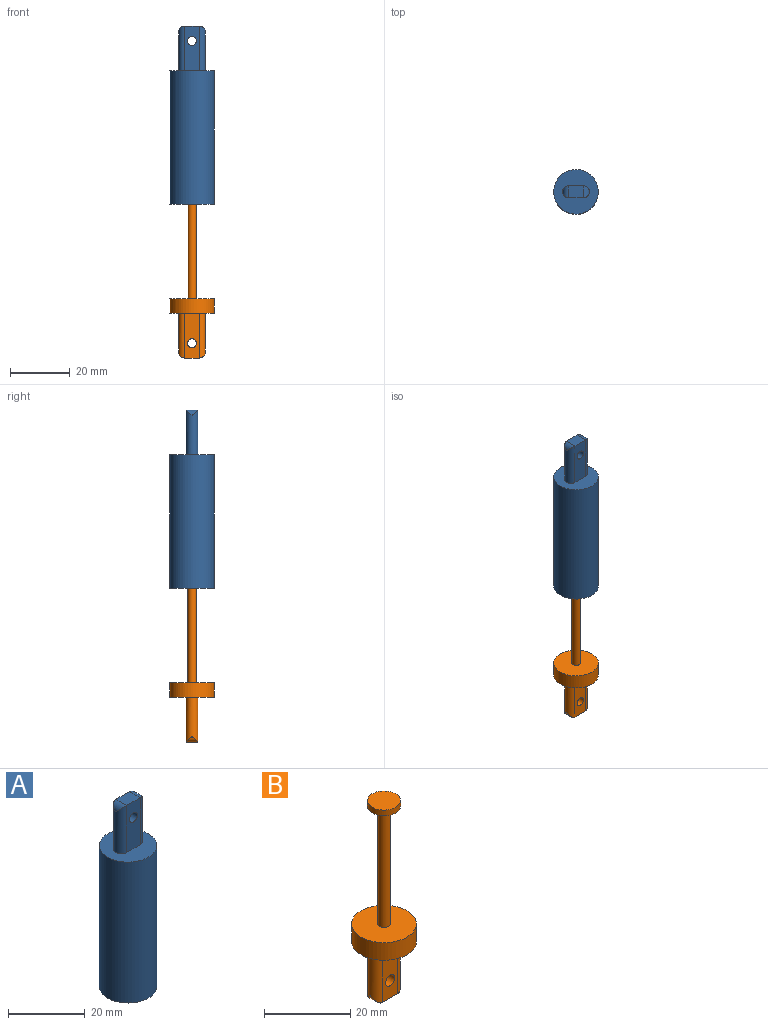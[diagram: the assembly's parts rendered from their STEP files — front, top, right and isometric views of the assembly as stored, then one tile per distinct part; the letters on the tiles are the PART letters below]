
ASSEMBLY  parts=2 mates=1
PART A: 15 faces, bbox 15x15x60 mm
  f0: cylinder r=7.5mm len=45mm, axis (0,0,1), area 2120.6mm2, adj f1,f6
  f1: plane 15x15mm, normal (0,0,1), area 144.1mm2, adj f0,f7,f8,f10,f13
  f2: plane 11.87x11.87mm, normal (0,0,-1), area 110.6mm2, adj f3
  f3: cylinder r=5.93mm len=41.52mm, axis (0,0,1), area 1547.7mm2, adj f2,f4
  f4: plane 11.87x11.87mm, normal (0,0,1), area 95.8mm2, adj f3,f5
  f5: cylinder r=2.17mm len=4.34mm, axis (0,0,1), area 24.1mm2, adj f4,f6
  f6: plane 15x15mm, normal (0,0,-1), area 161.9mm2, adj f0,f5
  f7: plane 15x5mm, normal (0,1,0), area 67.9mm2, adj f1,f9,f10,f13,f14
  f8: plane 15x5mm, normal (0,-1,0), area 67.9mm2, adj f1,f9,f10,f13,f14
  f9: plane 5x4mm, normal (0,0,1), area 20mm2, adj f7,f8,f11,f12
  f10: cylinder r=2mm len=15mm, axis (0,0,-1), area 89.7mm2, adj f1,f7,f8,f11
  f11: cylinder r=2mm len=4mm, axis (0,-1,0), area 8mm2, adj f9,f10
  f12: cylinder r=2mm len=4mm, axis (0,1,0), area 8mm2, adj f9,f13
  f13: cylinder r=2mm len=15mm, axis (0,0,1), area 89.7mm2, adj f1,f7,f8,f12
  f14: cylinder r=1.5mm len=4mm, axis (0,-1,0), area 37.7mm2, adj f7,f8
PART B: 15 faces, bbox 15x15x55 mm
  f0: cylinder r=3.83mm len=7.65mm, axis (0,0,1), area 38.9mm2, adj f1,f6
  f1: plane 7.65x7.65mm, normal (0,0,1), area 46mm2, adj f0
  f2: plane 15x15mm, normal (0,0,-1), area 144.1mm2, adj f3,f7,f8,f11,f12
  f3: cylinder r=7.5mm len=15mm, axis (0,0,1), area 235.6mm2, adj f2,f4
  f4: plane 15x15mm, normal (0,0,1), area 170.4mm2, adj f3,f5
  f5: cylinder r=1.42mm len=33.37mm, axis (0,0,1), area 297.7mm2, adj f4,f6
  f6: plane 7.65x7.65mm, normal (0,0,-1), area 39.7mm2, adj f0,f5
  f7: plane 15x5mm, normal (0,-1,0), area 67.9mm2, adj f2,f9,f11,f12,f14
  f8: plane 15x5mm, normal (0,1,0), area 67.9mm2, adj f2,f9,f11,f12,f14
  f9: plane 5x4mm, normal (0,0,-1), area 20mm2, adj f7,f8,f10,f13
  f10: cylinder r=2mm len=4mm, axis (0,1,0), area 8mm2, adj f9,f11
  f11: cylinder r=2mm len=15mm, axis (0,0,1), area 89.7mm2, adj f2,f7,f8,f10
  f12: cylinder r=2mm len=15mm, axis (0,0,-1), area 89.7mm2, adj f2,f7,f8,f13
  f13: cylinder r=2mm len=4mm, axis (0,-1,0), area 8mm2, adj f9,f12
  f14: cylinder r=1.5mm len=4mm, axis (0,-1,0), area 37.7mm2, adj f7,f8
PLACE A t=(-4.5,0,-58)mm
PLACE B t=(-4.5,0,-59.61)mm
MATE slider B.f0 <-> A.f0  axis (0,0,-1) through (-4.5,0,-56.24)mm
